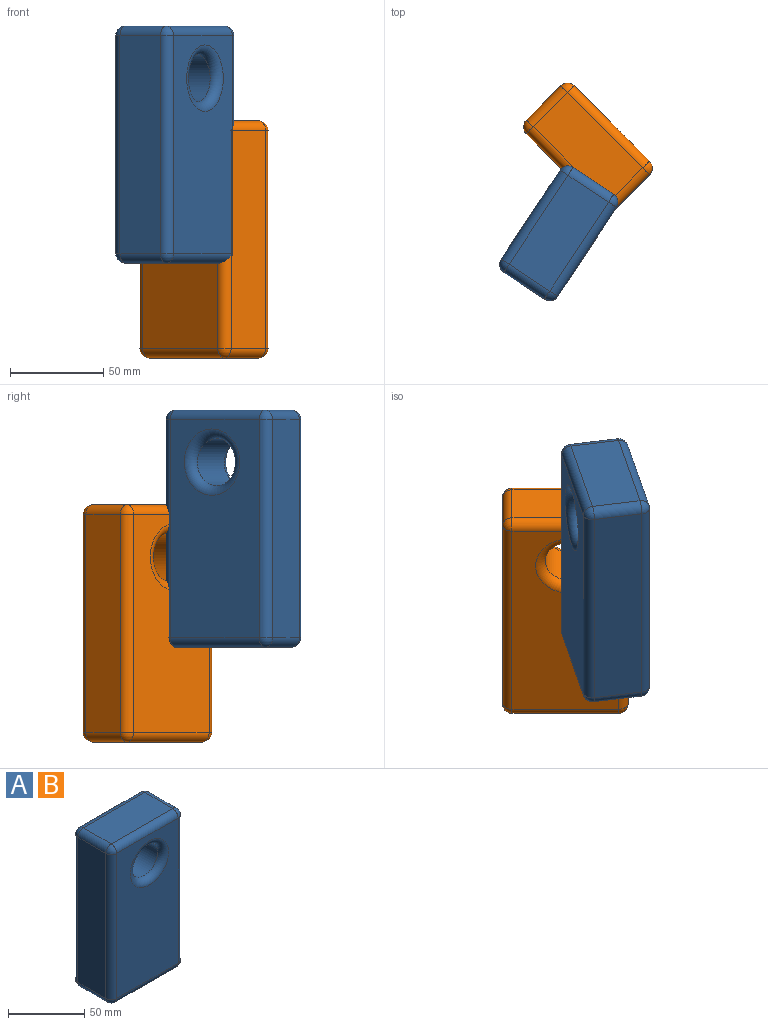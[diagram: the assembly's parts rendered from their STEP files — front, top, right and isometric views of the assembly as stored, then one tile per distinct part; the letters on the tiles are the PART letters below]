
ASSEMBLY  parts=2 mates=1
PART A: 29 faces, bbox 67.3x36.2x127 mm
  f0: plane 116.84x26mm, normal (-1,0,0), area 3038.2mm2, adj f17,f22,f25,f28
  f1: plane 116.84x57.1mm, normal (0,-1,0), area 5678.7mm2, adj f7,f14,f23,f24,f28
  f2: plane 116.84x26mm, normal (1,0,0), area 3038.2mm2, adj f9,f13,f14,f15
  f3: plane 116.84x57.1mm, normal (0,1,0), area 5678.7mm2, adj f8,f9,f12,f16,f17
  f4: plane 57.1x26mm, normal (0,0,1), area 1484.8mm2, adj f12,f13,f22,f23
  f5: plane 57.1x26mm, normal (0,0,-1), area 1484.8mm2, adj f15,f16,f24,f25
  f6: cylinder r=12.7mm len=26mm, axis (0,1,0), area 2074.9mm2, adj f7,f8
  f7: torus R=17.78mm, axis (0,1,0), area 729.3mm2, adj f1,f6
  f8: torus R=17.78mm, axis (0,1,0), area 729.3mm2, adj f3,f6
  f9: cylinder r=5.08mm len=116.84mm, axis (0,0,1), area 932.3mm2, adj f2,f3,f10,f11
  f10: sphere r=5.08mm, area 40.5mm2, adj f9,f12,f13
  f11: sphere r=5.08mm, area 40.5mm2, adj f9,f15,f16
  f12: cylinder r=5.08mm len=57.1mm, axis (1,0,0), area 455.7mm2, adj f3,f4,f10,f18
  f13: cylinder r=5.08mm len=26mm, axis (0,-1,0), area 207.5mm2, adj f2,f4,f10,f19
  f14: cylinder r=5.08mm len=116.84mm, axis (0,0,-1), area 932.3mm2, adj f1,f2,f19,f20
  f15: cylinder r=5.08mm len=26mm, axis (0,1,0), area 207.5mm2, adj f2,f5,f11,f20
  f16: cylinder r=5.08mm len=57.1mm, axis (-1,0,0), area 455.7mm2, adj f3,f5,f11,f21
  f17: cylinder r=5.08mm len=116.84mm, axis (0,0,-1), area 932.3mm2, adj f0,f3,f18,f21
  f18: sphere r=5.08mm, area 40.5mm2, adj f12,f17,f22
  f19: sphere r=5.08mm, area 40.5mm2, adj f13,f14,f23
  f20: sphere r=5.08mm, area 40.5mm2, adj f14,f15,f24
  f21: sphere r=5.08mm, area 40.5mm2, adj f16,f17,f25
  f22: cylinder r=5.08mm len=26mm, axis (0,1,0), area 207.5mm2, adj f0,f4,f18,f26
  f23: cylinder r=5.08mm len=57.1mm, axis (-1,0,0), area 455.7mm2, adj f1,f4,f19,f26
  f24: cylinder r=5.08mm len=57.1mm, axis (1,0,0), area 455.7mm2, adj f1,f5,f20,f27
  f25: cylinder r=5.08mm len=26mm, axis (0,-1,0), area 207.5mm2, adj f0,f5,f21,f27
  f26: sphere r=5.08mm, area 40.5mm2, adj f22,f23,f28
  f27: sphere r=5.08mm, area 40.5mm2, adj f24,f25,f28
  f28: cylinder r=5.08mm len=116.84mm, axis (0,0,1), area 932.3mm2, adj f0,f1,f26,f27
PART B: same geometry as A
PLACE A rot(axis=(0,0,1),56.6deg) t=(93.09,70.14,4.46)mm
PLACE B rot(axis=(0,0,-1),45deg) t=(103.11,112.68,-46.34)mm fixed
MATE revolute B.f14 <-> A.f14  axis (0,0,-1) through (115.45,87.32,-46.34)mm
